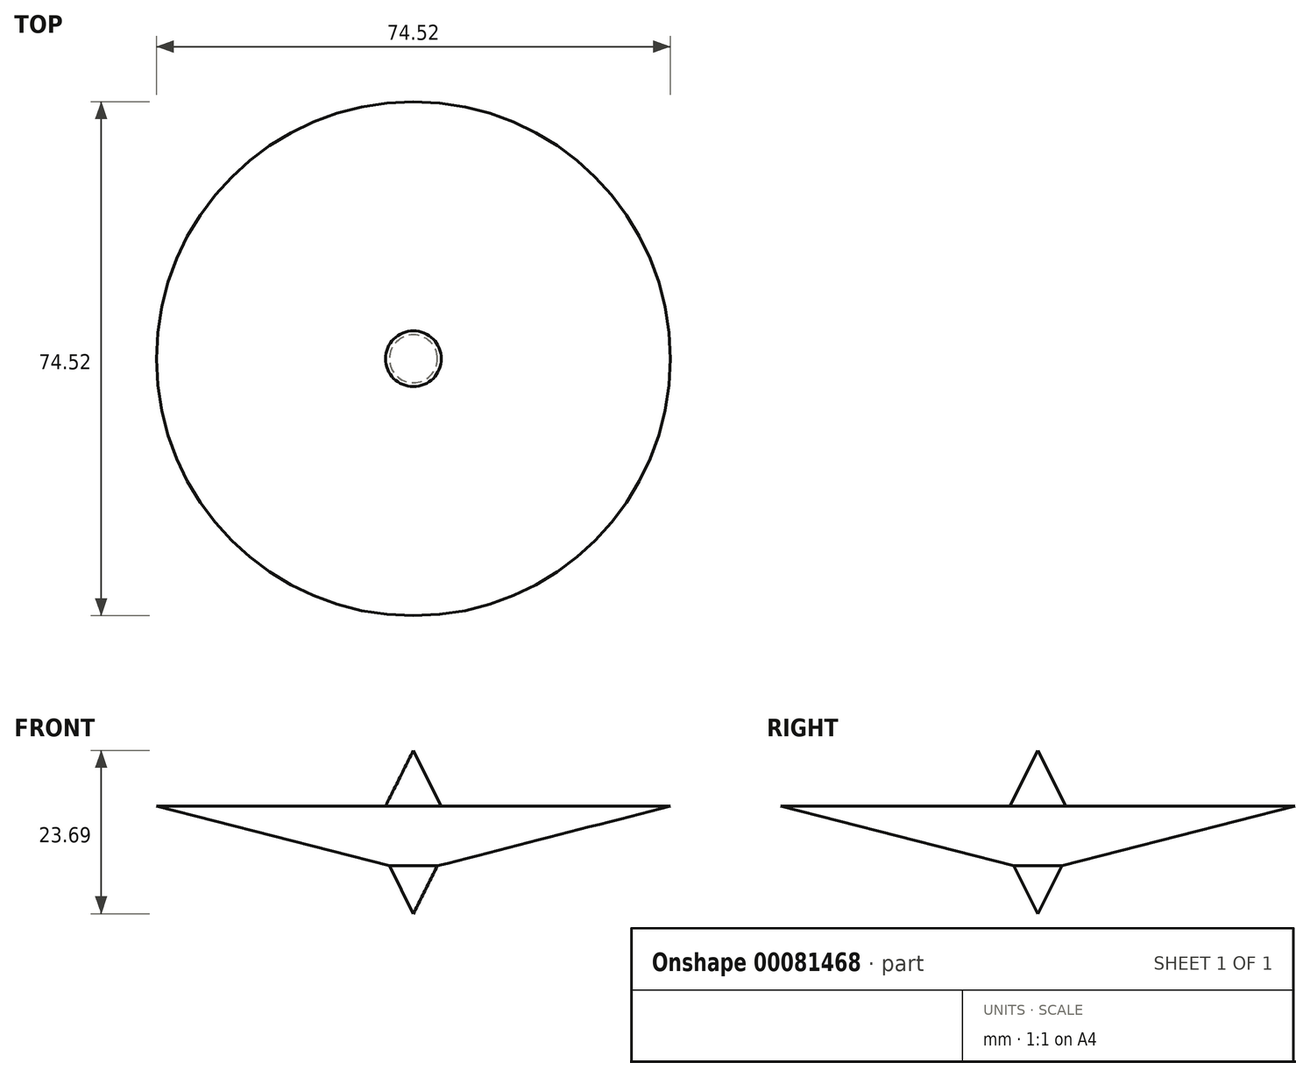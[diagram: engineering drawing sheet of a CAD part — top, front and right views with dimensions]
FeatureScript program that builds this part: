
annotation { "Feature Type Name" : "Feature", "Feature Type Description" : "" }
export const myFeature = defineFeature(function(context is Context, id is Id, definition is map)
    precondition{}
    {
        {
            var Q0;
            Q0=qCreatedBy(makeId("Front.planeOp"),FACE);
            var sketch = newSketch(context, id + "F0", { "sketchPlane" : qUnion([Q0])});
            skLineSegment(sketch, "E0", {"start": v(0, 0) * mm, "end": v(3.47, 6.93) * mm});
            skLineSegment(sketch, "E1", {"start": v(3.47, 6.93) * mm, "end": v(37.26, 15.6) * mm});
            skLineSegment(sketch, "E2", {"start": v(37.26, 15.6) * mm, "end": v(4.04, 15.6) * mm});
            skLineSegment(sketch, "E3", {"start": v(4.04, 15.6) * mm, "end": v(0, 23.69) * mm});
            skLineSegment(sketch, "E4", {"start": v(0, 23.69) * mm, "end": v(0, 0) * mm});
            skSolve(sketch);
        }
        {
            var Q0;
            Q0=makeQuery(id+"F0.imprint","IMPRINT",FACE,{"disambiguationData":[TD([[makeQuery(id+"F0.imprint","IMPRINT",EDGE,{"derivedFrom":sQuery(id+"F0.wireOp",EDGE,"E0")}),1.0]])]});
            var Q1;
            Q1=sQuery(id+"F0.wireOp",EDGE,"E4");
            revolve(context, id + "F1", {"entities" : qUnion([Q0]), "axis" : qUnion([Q1]), "revolveType" : RevolveType.FULL});
        }
    });
